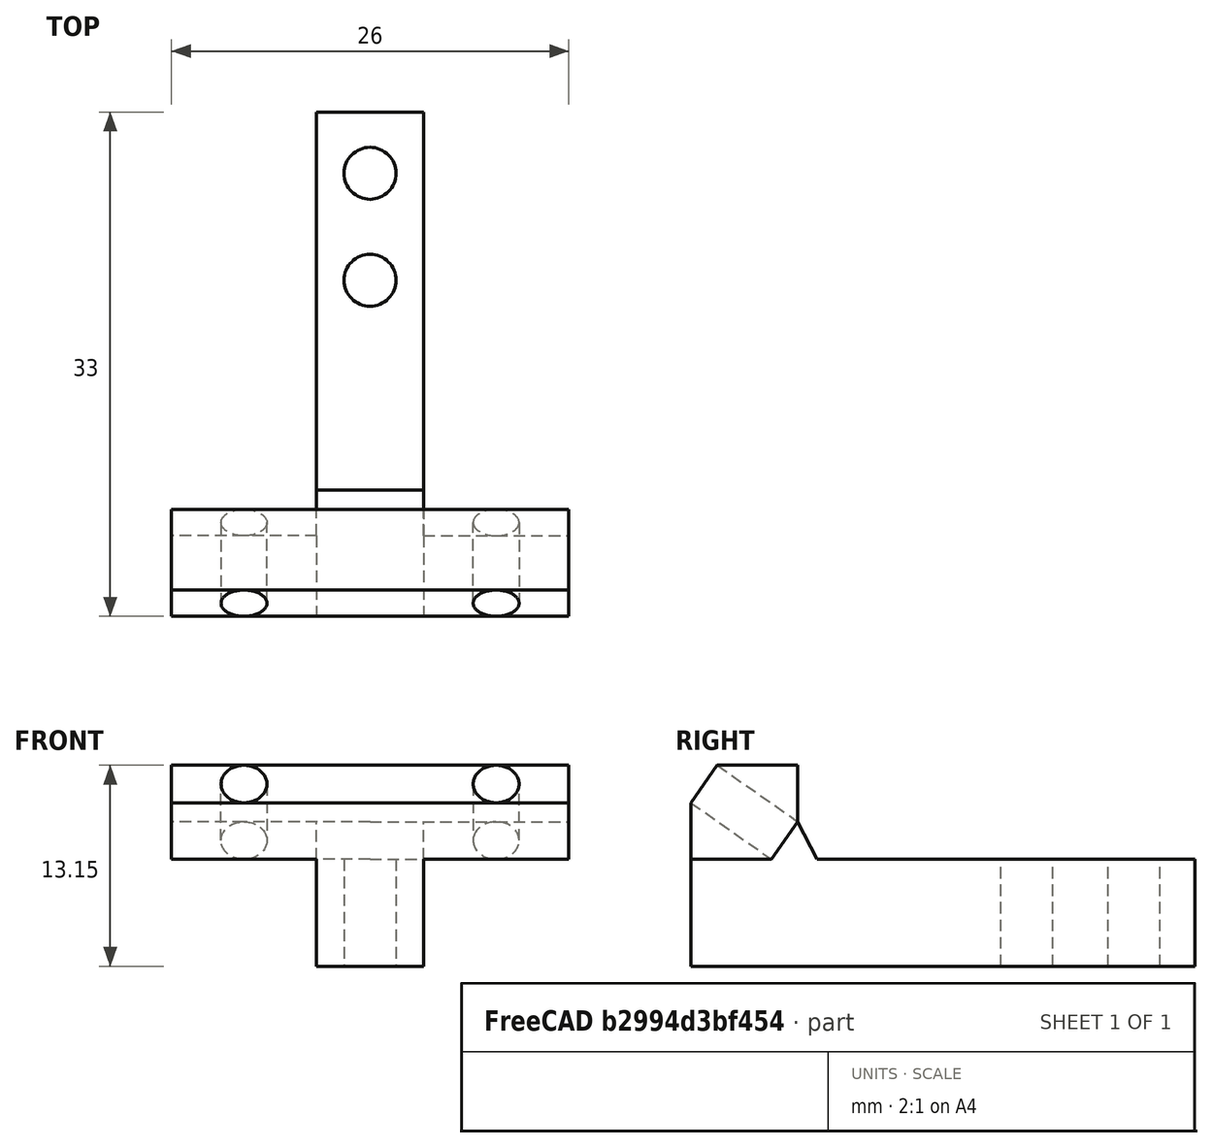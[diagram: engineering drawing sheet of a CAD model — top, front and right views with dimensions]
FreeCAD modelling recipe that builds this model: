
FCSTD DOCUMENT  (FreeCAD 0.19R24291 (Git))
Label: Иголки 70 1
License: All rights reserved
LicenseURL: http://en.wikipedia.org/wiki/All_rights_reserved
objects: Sketcher::SketchObject×5, Mesh::Feature×2, PartDesign::Pad×2, PartDesign::Pocket×1, PartDesign::Chamfer×1, PartDesign::Mirrored×1, PartDesign::Body×1
note: 15 computed .brp shape members not serialized (recipe doc carries the construction recipe); baked Part::Feature solids carry a one-line shape summary decoded from their .brp

FEATURE [Mesh::Feature] _5Angle  label="45Angle"
FEATURE [Sketcher::SketchObject] Sketch
  FullyConstrained = true
  MapMode = 5
  Support = -> [XY_Plane]
  sketch-geometry (8):
    g0: ArcOfCircle CenterX=0 CenterY=22 CenterZ=0 NormalX=0 NormalY=0 NormalZ=1 AngleXU=0 Radius=1.7 StartAngle=1.5708 EndAngle=4.71239
    g1: ArcOfCircle CenterX=0 CenterY=29 CenterZ=0 NormalX=0 NormalY=0 NormalZ=1 AngleXU=0 Radius=1.7 StartAngle=1.5708 EndAngle=4.71239
    g2: LineSegment StartX=1e-16 StartY=30.7 StartZ=0 EndX=0 EndY=33 EndZ=0
    g3: LineSegment StartX=0 StartY=33 StartZ=0 EndX=-3.5 EndY=33 EndZ=0
    g4: LineSegment StartX=-3.5 StartY=33 StartZ=0 EndX=-3.5 EndY=0 EndZ=0
    g5: LineSegment StartX=-3.5 StartY=0 StartZ=0 EndX=0 EndY=0 EndZ=0
    g6: LineSegment StartX=0 StartY=0 StartZ=0 EndX=0 EndY=20.3 EndZ=0
    g7: LineSegment StartX=-3e-16 StartY=27.3 StartZ=0 EndX=1e-16 EndY=23.7 EndZ=0
  constraints (26):
    c: PointOnObject(g0,g-2)
    c: PointOnObject(g0,g-2)
    c: PointOnObject(g0,g-2)
    c: PointOnObject(g1,g-2)
    c: PointOnObject(g1,g-2)
    c: PointOnObject(g1,g-2)
    c: Distance(g0,g1) = 7
    c: Distance(g0,g-1) = 22
    c: Equal(g0,g1)
    c: Diameter(g0) = 3.4
    c: Coincident(g2,g1)
    c: PointOnObject(g2,g-2)
    c: Coincident(g2,g3)
    c: Horizontal(g3)
    c: Coincident(g3,g4)
    c: PointOnObject(g4,g-1)
    c: Vertical(g4)
    c: Coincident(g4,g5)
    c: Coincident(g5,g-1)
    c: Coincident(g5,g6)
    c: Coincident(g6,g0)
    c: Distance(g2) = 2.3
    c: Distance(g3) = 3.5
    c: Coincident(g7,g1)
    c: Coincident(g7,g0)
    c: Distance(g4) = 33
FEATURE [PartDesign::Pad] Pad
  Direction = (1,1,1)
  Length = 7
  Length2 = 100
  Profile = -> Sketch
  Type = 0
FEATURE [Sketcher::SketchObject] Sketch003
  FullyConstrained = true
  MapMode = 5
  Placement = pos=(-3.5,0,0) rot=(0.57735,-0.57735,-0.57735;2.0944rad)
  Support = -> [Pad]
  sketch-geometry (4):
    g0: LineSegment StartX=0 StartY=0 StartZ=0 EndX=7.07107 EndY=7.07107 EndZ=0
    g1: LineSegment StartX=7.07107 StartY=7.07107 StartZ=0 EndX=0.707107 EndY=13.435 EndZ=0
    g2: LineSegment StartX=0.707107 StartY=13.435 StartZ=0 EndX=-6.36396 EndY=6.36396 EndZ=0
    g3: LineSegment StartX=-6.36396 StartY=6.36396 StartZ=0 EndX=0 EndY=0 EndZ=0
  constraints (11):
    c: Coincident(g-1,g0)
    c: Coincident(g0,g1)
    c: Coincident(g1,g2)
    c: Coincident(g2,g3)
    c: Coincident(g3,g0)
    c: Perpendicular(g1,g0)
    c: Perpendicular(g3,g0)
    c: Perpendicular(g2,g3)
    c: Angle(g-1,g0) = 0.785398
    c: Distance(g0) = 10
    c: Distance(g3) = 9
FEATURE [Sketcher::SketchObject] Sketch004
  FullyConstrained = false
  MapMode = 5
  Placement = pos=(0,6.36396,6.36396) rot=(0,0.382683,0.92388;3.14159rad)
  sketch-geometry (3):
    g0: Circle CenterX=7.5 CenterY=5 CenterZ=0 NormalX=0 NormalY=0 NormalZ=1 AngleXU=0 Radius=1
    g1: LineSegment StartX=0 StartY=10 StartZ=0 EndX=7.5 EndY=5 EndZ=0
    g2: LineSegment StartX=7.5 StartY=5 StartZ=0 EndX=0 EndY=0 EndZ=0
  constraints (6):
    c: Coincident(g1,g0)
    c: Coincident(g2,g0)
    c: Coincident(g2,g-1)
    c: Equal(g2,g1)
    c: Distance(g0,g-2) = 7.5
    c: Diameter(g0) = 2
FEATURE [Sketcher::SketchObject] Sketch005
  FullyConstrained = true
  MapMode = 5
  Placement = pos=(-3.5,0,0) rot=(0.57735,-0.57735,-0.57735;2.0944rad)
  Support = -> [Pad]
  sketch-geometry (8):
    g0: LineSegment StartX=0 StartY=7 StartZ=0 EndX=-5.27927 EndY=7 EndZ=0
    g1: LineSegment StartX=-7 StartY=9.45746 StartZ=0 EndX=-7 EndY=13.154 EndZ=0
    g2: LineSegment StartX=-7 StartY=13.154 StartZ=0 EndX=-1.72073 EndY=13.154 EndZ=0
    g3: LineSegment StartX=0 StartY=10.6966 StartZ=0 EndX=0 EndY=7 EndZ=0
    g4: LineSegment StartX=-1.72073 StartY=13.154 StartZ=0 EndX=0 EndY=10.6966 EndZ=0
    g5: LineSegment StartX=-7 StartY=9.45746 StartZ=0 EndX=-5.27927 EndY=7 EndZ=0
    g6: LineSegment StartX=-7 StartY=9.45746 StartZ=0 EndX=-1.72073 EndY=13.154 EndZ=0
    g7: LineSegment StartX=0 StartY=10.6966 StartZ=0 EndX=-5.27927 EndY=7 EndZ=0
  constraints (22):
    c: Coincident(g1,g2)
    c: Horizontal(g0)
    c: Horizontal(g2)
    c: Vertical(g1)
    c: Coincident(g6,g5)
    c: Coincident(g6,g4)
    c: Coincident(g7,g4)
    c: Coincident(g7,g5)
    c: Distance(g4) = 3
    c: Coincident(g2,g4)
    c: Coincident(g3,g4)
    c: Coincident(g0,g5)
    c: Coincident(g1,g5)
    c: Distance(g1,g-2) = 7
    c: PointOnObject(g3,g-2)
    c: Coincident(g0,g3)
    c: PointOnObject(g0,g-2)
    c: Distance(g0,g-1) = 7
    c: Angle(g7,g3) = 0.959931
    c: Perpendicular(g7,g4)
    c: Perpendicular(g5,g6)
    c: Perpendicular(g7,g5)
FEATURE [PartDesign::Pad] Pad001
  BaseFeature = -> Pad
  Direction = (1,1,1)
  Length = 9.5
  Length2 = 3.5
  Profile = -> Sketch005
  Type = 4
FEATURE [Sketcher::SketchObject] Sketch006
  ExternalGeometry = -> [Pad001]
  FullyConstrained = true
  MapMode = 5
  Placement = pos=(0,0.25352,-0.177516) rot=(0,0.887011,0.461749;3.14159rad)
  Support = -> [Pad001]
  sketch-geometry (3):
    g0: LineSegment StartX=13 StartY=11.7621 StartZ=0 EndX=3.5 EndY=8.76213 EndZ=0
    g1: LineSegment StartX=3.5 StartY=11.7621 StartZ=0 EndX=13 EndY=8.76213 EndZ=0
    g2: Circle CenterX=8.25 CenterY=10.2621 CenterZ=0 NormalX=0 NormalY=0 NormalZ=1 AngleXU=0 Radius=1.5
  constraints (8):
    c: PointOnObject(g2,g0)
    c: PointOnObject(g2,g1)
    c: Diameter(g2) = 3
    c: Coincident(g0,g-4)
    c: Coincident(g0,g-3)
    c: Coincident(g1,g-3)
    c: PointOnObject(g1,g-4)
    c: Vertical(g1,g0)
FEATURE [PartDesign::Pocket] Pocket
  BaseFeature = -> Pad001
  Length = 5
  Length2 = 100
  Profile = -> Sketch006
  Type = 1
FEATURE [PartDesign::Chamfer] Chamfer
  Angle = 45
  Base = -> Pocket [Edge18]
  BaseFeature = -> Pocket
  ChamferType = 0
  FlipDirection = false
  Size = 2.99
  Size2 = 1
  SupportTransform = false
FEATURE [PartDesign::Mirrored] Mirrored
  BaseFeature = -> Chamfer
  MirrorPlane = -> Sketch [V_Axis]
  Originals = -> [Pad,Pad001,Pocket,Chamfer]
FEATURE [PartDesign::Body] Body
  Group = -> [Sketch,Pad,Sketch003,Sketch004,Sketch005,Pad001,Sketch006,Pocket,Chamfer,Mirrored]
  Origin = -> Origin
  Tip = -> Mirrored
FEATURE [Mesh::Feature] ____________2  label="Иголки2"
